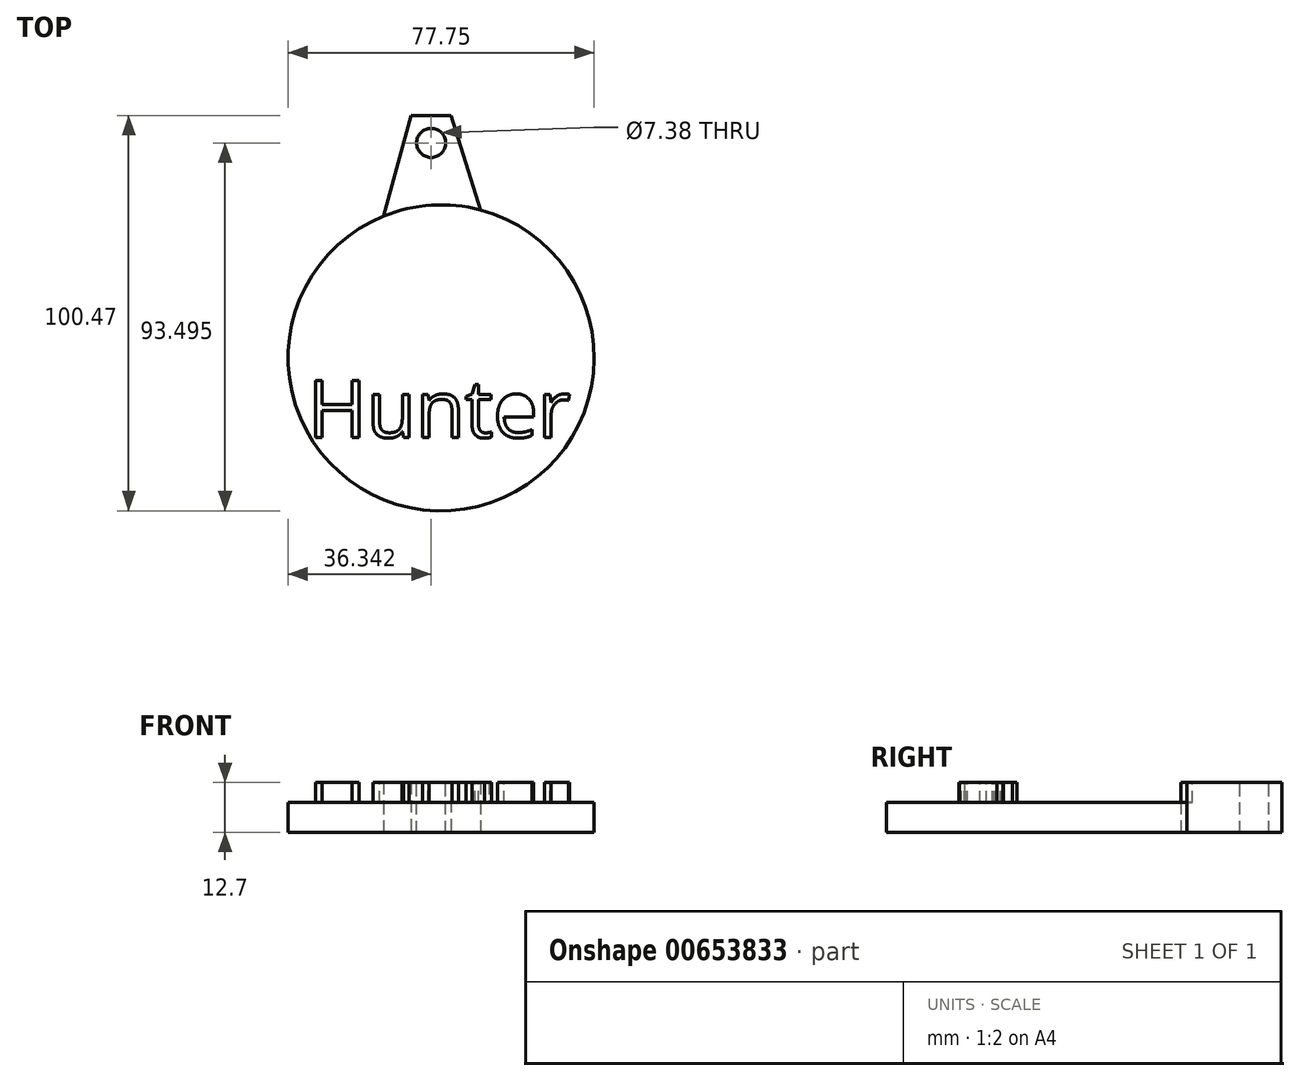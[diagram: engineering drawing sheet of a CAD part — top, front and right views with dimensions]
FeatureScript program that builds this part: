
annotation { "Feature Type Name" : "Feature", "Feature Type Description" : "" }
export const myFeature = defineFeature(function(context is Context, id is Id, definition is map)
    precondition{}
    {
        {
            var Q0;
            Q0=qCreatedBy(makeId("Top.planeOp"),FACE);
            var sketch = newSketch(context, id + "F0", { "sketchPlane" : qUnion([Q0])});
            skArc(sketch, "E0", {"start": v(-61.2, 56.23) * mm, "mid": v(-44.11, -18.58) * mm, "end": v(-36.6, 57.79) * mm});
            skLineSegment(sketch, "E1", {"start": v(-61.2, 56.23) * mm, "end": v(-54.2, 81.8) * mm});
            skLineSegment(sketch, "E2", {"start": v(-54.2, 81.8) * mm, "end": v(-44.03, 81.8) * mm});
            skLineSegment(sketch, "E3", {"start": v(-44.03, 81.8) * mm, "end": v(-36.6, 57.79) * mm});
            skPoint(sketch, "E4.orphan", {"position": v(-33.87, 81.8) * mm});
            skSolve(sketch);
        }
        {
            var Q0;
            Q0=makeQuery(id+"F0.imprint","IMPRINT",FACE,{"disambiguationData":[TD([[makeQuery(id+"F0.imprint","IMPRINT",EDGE,{"derivedFrom":sQuery(id+"F0.wireOp",EDGE,"E0")}),1.0]])]});
            extrude(context, id + "F1", {"entities" : qUnion([Q0]), "depth" : 12.7 * mm, "offsetDistance" : 25.4 * mm});
        }
        {
            var Q0;
            Q0=makeQuery(id+"F1.opExtrude","CAP_FACE",FACE,{"disambiguationData":[OSD([sQuery(id+"F0.wireOp",EDGE,"E0"),sQuery(id+"F0.wireOp",EDGE,"E1"),sQuery(id+"F0.wireOp",EDGE,"E2"),sQuery(id+"F0.wireOp",EDGE,"E3")])],"isStart":false});
            var sketch = newSketch(context, id + "F2", { "sketchPlane" : qUnion([Q0])});
            skCircle(sketch, "E5", {"center": v(-46.57, 20.21) * mm, "radius": 38.88 * mm});
            skCircle(sketch, "E6", {"center": v(-49.1, 74.84) * mm, "radius": 3.7 * mm});
            skText(sketch, "E7", { "text": "Hunter", "fontName": "OpenSans-Regular.ttf"});
            const initialGuessF2  = {"E7": [-0.08047, 0, 1, 0, 0.01462]};
            skSetInitialGuess(sketch, initialGuessF2);
            skSolve(sketch);
        }
        {
            var Q0;
            Q0=makeQuery(id+"F2.imprint","IMPRINT",FACE,{"disambiguationData":[TD([[makeQuery(id+"F2.imprint","IMPRINT",EDGE,{"derivedFrom":sQuery(id+"F2.wireOp",EDGE,"E5")}),1.0]])]});
            extrude(context, id + "F3", {"entities" : qUnion([Q0]), "operationType" : NewBodyOperationType.REMOVE, "oppositeDirection" : true, "depth" : 5.08 * mm, "offsetDistance" : 25.4 * mm});
        }
        {
            var Q0;
            Q0=makeQuery(id+"F2.imprint","IMPRINT",FACE,{"disambiguationData":[TD([[makeQuery(id+"F2.imprint","IMPRINT",EDGE,{"derivedFrom":sQuery(id+"F2.wireOp",EDGE,"E6")}),1.0]])]});
            extrude(context, id + "F4", {"entities" : qUnion([Q0]), "operationType" : NewBodyOperationType.REMOVE, "endBound" : BoundingType.THROUGH_ALL, "oppositeDirection" : true, "depth" : 25.4 * mm, "offsetDistance" : 25.4 * mm});
        }
    });
